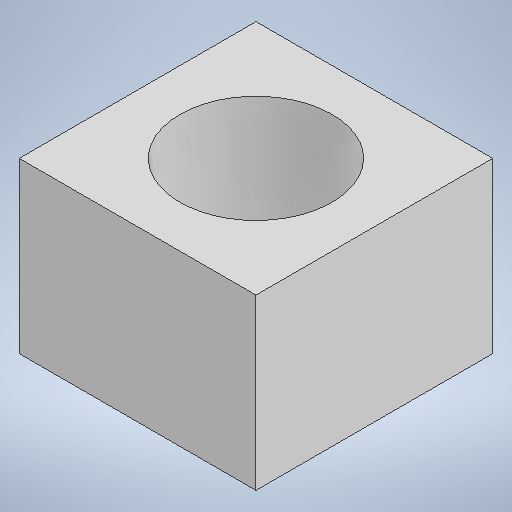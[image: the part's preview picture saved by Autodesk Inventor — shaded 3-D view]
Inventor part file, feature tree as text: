
AUTODESK INVENTOR PART (.ipt)
format: ipt  version: 2025 (Build 290162000, 162)  size: 155,648 bytes
history: native  units: mm
features: extrude x1, sketch x1
ambient origin geometry x8: Origin, YZ Plane, XZ Plane, XY Plane, X Axis, Y Axis, Z Axis, Center Point
bodies: Solid1 (feature_tree)
feature tree (2):
  extrude  "Extrusion1"  Depth=7.0mm
  sketch  "Sketch1"  dims[d0=4.5mm d1=7.0mm d2=7.0mm d3=5.0mm d4=0.0mm]
